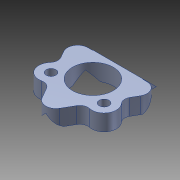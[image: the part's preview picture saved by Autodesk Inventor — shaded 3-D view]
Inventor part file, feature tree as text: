
AUTODESK INVENTOR PART (.ipt)
format: ipt  version: 2011 (Build 150239000, 239)  size: 573,440 bytes
history: native  units: in
note: dims shown in document units (in); Inventor stores cm internally (conversion verified against a paired STEP export)
features: sketch x4, hole x2, other x1, imported_body x1, extrude x1, draft x1, emboss x1, fillet x1
ambient origin geometry x8: Origin, YZ Plane, XZ Plane, XY Plane, X Axis, Y Axis, Z Axis, Center Point
feature tree (12):
  other  "TricornerSeat"
  imported_body  "Base1"
  extrude  "Extrusion1"  TaperAngle=45.0deg  [1 undecoded]
  draft  "FaceDraft1"
  emboss  "Emboss1"
  sketch  "Sketch4"  dims[d21=0.0394in d22=0.0394in d23=0.002in]
  sketch  "Sketch5"  dims[d24=0.002in d25=3.937in d27=0.0394in d28=1.9685in d30=0.0394in d33=0.0039in d34=0.0in d35=0.0945in d36=0.2362in d37=0.1732in d38=0.0787in d39=90.0deg d40=0.315in d41=0.8108in d42=0.0945in d43=0.2362in d44=0.1732in d45=0.0787in d46=90.0deg d47=0.315in d48=0.8108in d49=0.0394in]
  hole  "Hole1"  [1 undecoded]
  hole  "Hole2"  [1 undecoded]
  fillet  "Fillet1"  Radius=0.002in
  sketch  "Sketch1"  dims[d0=0.0039in d1=0.0in d2=45.0deg]
  sketch  "Sketch3"  dims[d19=0.1969in d20=0.0984in]
note: 3 required parameter values undecoded (feature->parameter linkage not recoverable at this tier; creation-order binding heuristic only, values carry confidence <= 0.55)
